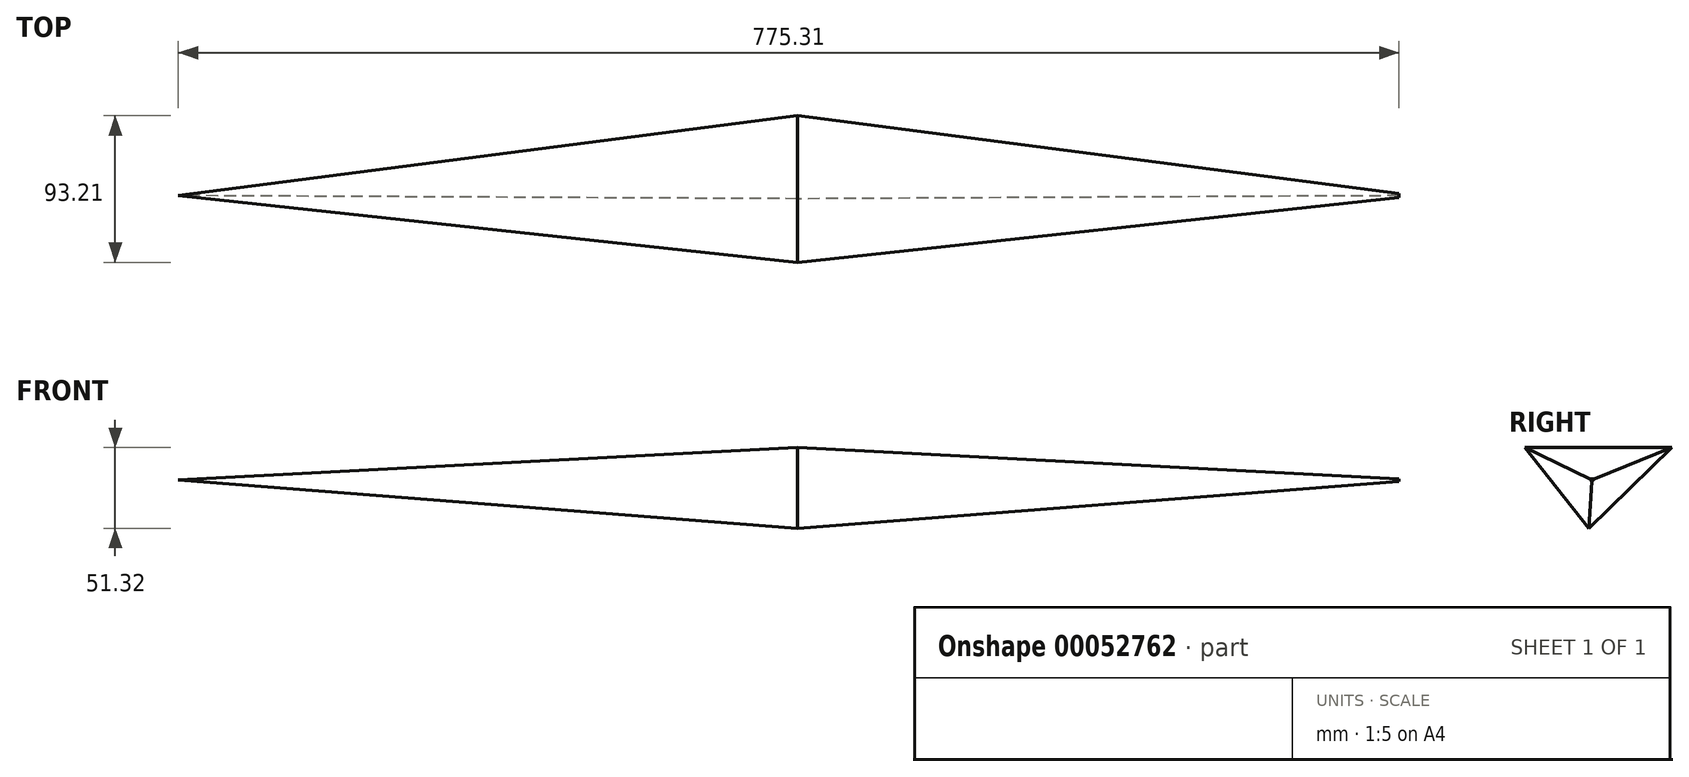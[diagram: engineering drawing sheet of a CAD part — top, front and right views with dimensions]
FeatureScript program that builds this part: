
annotation { "Feature Type Name" : "Feature", "Feature Type Description" : "" }
export const myFeature = defineFeature(function(context is Context, id is Id, definition is map)
    precondition{}
    {
        {
            var Q0;
            Q0=qCreatedBy(makeId("Right.planeOp"),FACE);
            var sketch = newSketch(context, id + "F0", { "sketchPlane" : qUnion([Q0])});
            skLineSegment(sketch, "E0", {"start": v(-40.38, 24.75) * mm, "end": v(52.83, 24.75) * mm});
            skLineSegment(sketch, "E1", {"start": v(52.83, 24.75) * mm, "end": v(0, -26.57) * mm});
            skLineSegment(sketch, "E2", {"start": v(0, -26.57) * mm, "end": v(-40.38, 24.75) * mm});
            skSolve(sketch);
        }
        {
            var Q0;
            Q0 = qSketchRegion(id + "F0", true);
            extrude(context, id + "F1", {"entities" : qUnion([Q0]), "depth" : 382.17 * mm, "hasDraft" : true, "draftAngle" : 3 * degree, "draftPullDirection" : true, "hasSecondDirection" : true, "secondDirectionOppositeDirection" : true, "secondDirectionDepth" : 712.9 * mm, "hasSecondDirectionDraft" : true, "secondDirectionDraftAngle" : 3 * degree, "secondDirectionDraftPullDirection" : true});
        }
    });
